# Revit family: NaughtOne_SymbolTwoSeatWork
name_source: partatom
category: Furniture
units: mm (PartAtom-declared; Revit-internal decimal feet)

## family parameters
Always vertical = Yes
Cut with Voids When Loaded = No
Enable Cutting in Views = No
OmniClass Number = 23.40.20.00
OmniClass Title = General Furniture and Specialties
Render Appearance Source = Family Geometry
Room Calculation Point = No
Shared = Yes
Work Plane-Based = No

## types (9) — shared parameters
Assembly Code = E2020200
Manufacturer = Herman Miller, Inc.
Package Qty = 1
URL = http://www.hermanmiller.com
zero-valued in all types: Default Elevation

## per-type parameters (varying)
| type | Description | Foot aux 1 | Foot aux 2 | Model | Seat Aux 1 | Seat Aux 2 | Seat Bench Single Fabric | Seat Left Arm Single and Multiple Fabric | Seat No Arms Single and Multiple Fabric | Seat Right Arm Single and Multiple Fabric | Seat Two Arms Single and Multiple Fabric | Type |
| Seat Bench Single Fabric Work Ht | Symbol Two Seat Bench Work height 18 inch seat height Single Fabric | 9.634 " | 19.55 " | NOSYN210W1 | 25 " | 25 " | Yes | No | No | No | No | 1 |
| Seat No Arms Single Fabric Work Ht | Symbol Two Seat No Arms Work height 18 inch seat height Single Fabric | 13.2 " | 19.55 " | NOSYN220W1 | 25 " | 21.5 " | No | No | Yes | No | No | 2 |
| Seat No Arms Multiple Fabric Work Ht | Symbol Two Seat No Arms Work height 18 inch seat height Multiple Fabric | 13.2 " | 19.55 " | NOSYN220W2 | 25 " | 21.5 " | No | No | Yes | No | No | 3 |
| Seat Right Arm Single Fabric Work Ht | Symbol Two Seat Right Arm Work height 18 inch seat height Single Fabric | 13.2 " | 23.1 " | NOSYN230W1 | 28.6 " | 21.5 " | No | Yes | No | No | No | 4 |
| Seat Right Arm Multiple Fabric Work Ht | Symbol Two Seat Right Arm Work height 18 inch seat height Multiple Fabric | 13.2 " | 23.1 " | NOSYN230W2 | 28.6 " | 21.5 " | No | Yes | No | No | No | 5 |
| Seat Left Arm Single Fabric Work Ht | Symbol Two Seat Left Arm Work height 18 inch seat height Single Fabric | 13.2 " | 23.1 " | NOSYN240W1 | 21.4 " | 21.5 " | No | No | No | Yes | No | 6 |
| Seat Left Arm Multiple Fabric Work Ht | Symbol Two Seat Left Arm Work height 18 inch seat height Multiple Fabric | 13.2 " | 23.1 " | NOSYN240W2 | 21.4 " | 21.5 " | No | No | No | Yes | No | 7 |
| Seat Two Arms Single Fabric Work Ht | Symbol Two Seat Two Arms Work height 18 inch seat height Single Fabric | 13.2 " | 26.65 " | NOSYN250W1 | 25 " | 21.5 " | No | No | No | No | Yes | 8 |
| Seat Two Arms Multiple Fabric Work Ht | Symbol Two Seat Two Arms Work height 18 inch seat height Multiple Fabric | 13.2 " | 26.65 " | NOSYN250W2 | 25 " | 21.5 " | No | No | No | No | Yes | 9 |

## geometry (parser evidence)
native form markers: Sweep x9
no freeform markers — native parametric forms only
